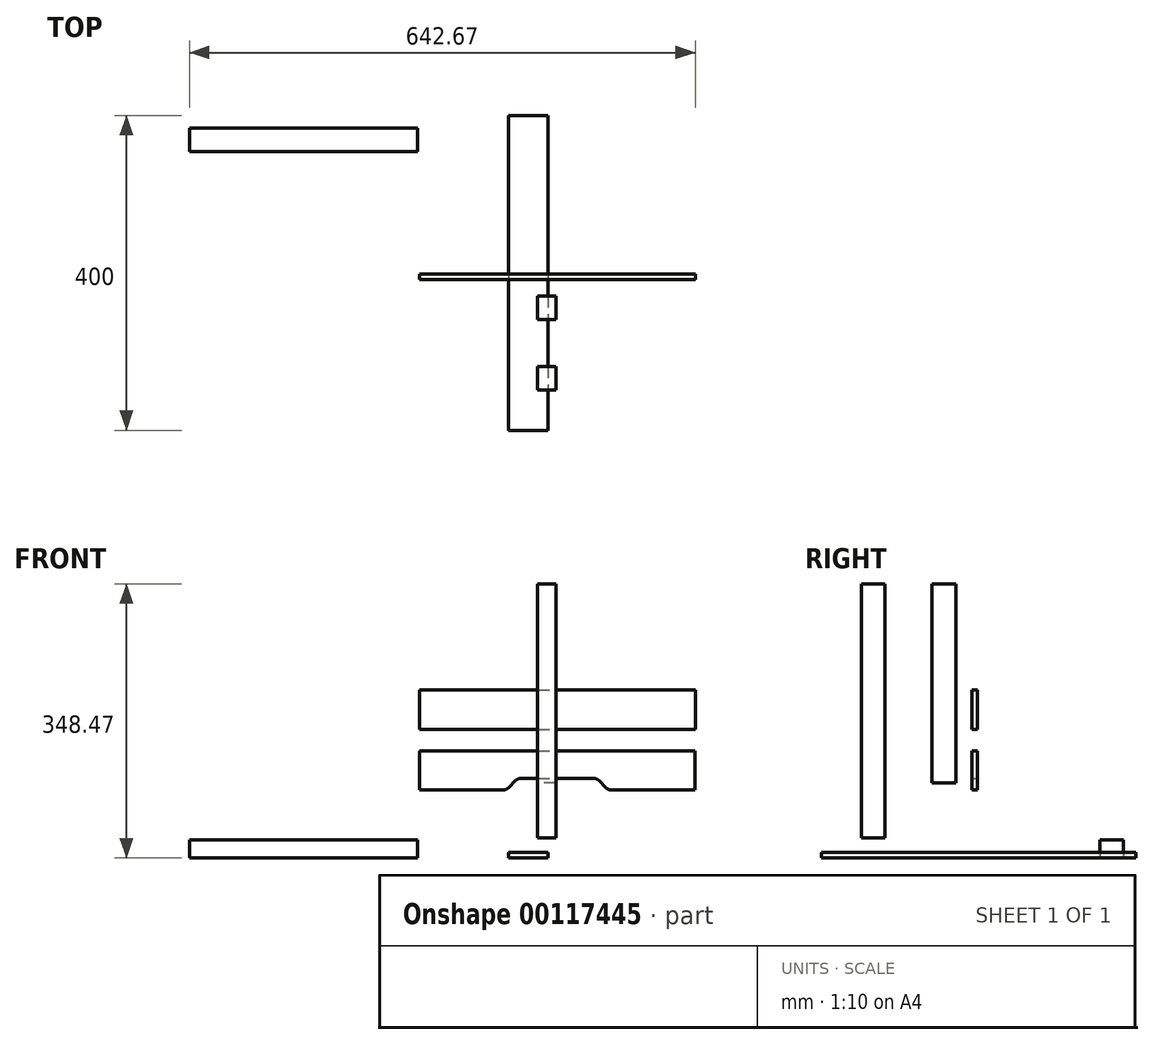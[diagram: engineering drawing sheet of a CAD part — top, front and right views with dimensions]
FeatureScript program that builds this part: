
annotation { "Feature Type Name" : "Feature", "Feature Type Description" : "" }
export const myFeature = defineFeature(function(context is Context, id is Id, definition is map)
    precondition{}
    {
        {
            var Q0;
            Q0=qCreatedBy(makeId("Top.planeOp"),FACE);
            var sketch = newSketch(context, id + "F0", { "sketchPlane" : qUnion([Q0])});
            skLineSegment(sketch, "E0.bottom", {"start": v(-36.82, 201.44) * mm, "end": v(13.18, 201.44) * mm});
            skLineSegment(sketch, "E0.top", {"start": v(-36.82, -198.56) * mm, "end": v(13.18, -198.56) * mm});
            skLineSegment(sketch, "E0.left", {"start": v(-36.82, 201.44) * mm, "end": v(-36.82, -198.56) * mm});
            skLineSegment(sketch, "E0.right", {"start": v(13.18, 201.44) * mm, "end": v(13.18, -198.56) * mm});
            skSolve(sketch);
        }
        {
            var Q0;
            Q0=makeQuery(id+"F2.imprint","IMPRINT",FACE,{"disambiguationData":[TD([[makeQuery(id+"F2.imprint","IMPRINT",EDGE,{"derivedFrom":sQuery(id+"F2.wireOp",EDGE,"E1.bottom")}),-1.0]])]});
            var Q1;
            Q1=makeQuery(id+"F0.imprint","IMPRINT",FACE,{"disambiguationData":[TD([[makeQuery(id+"F0.imprint","IMPRINT",EDGE,{"derivedFrom":sQuery(id+"F0.wireOp",EDGE,"E0.bottom")}),-1.0]])]});
            var Q2;
            Q2=sQuery(id+"F2.wireOp",EDGE,"E1.top");
            extrude(context, id + "F1", {"entities" : qUnion([Q0, Q1]), "surfaceEntities" : qUnion([Q2]), "depth" : 7 * mm});
        }
        {
            var Q0;
            Q0=qCreatedBy(makeId("Front.planeOp"),FACE);
            var sketch = newSketch(context, id + "F2", { "sketchPlane" : qUnion([Q0])});
            skLineSegment(sketch, "E1.bottom", {"start": v(-149.81, 213.54) * mm, "end": v(200.19, 213.54) * mm});
            skLineSegment(sketch, "E1.top", {"start": v(-149.81, 163.54) * mm, "end": v(200.19, 163.54) * mm});
            skLineSegment(sketch, "E1.left", {"start": v(-149.81, 213.54) * mm, "end": v(-149.81, 163.54) * mm});
            skLineSegment(sketch, "E1.right", {"start": v(200.19, 213.54) * mm, "end": v(200.19, 163.54) * mm});
            skLineSegment(sketch, "E2.bottom", {"start": v(-150.22, 136.45) * mm, "end": v(199.78, 136.45) * mm});
            skLineSegment(sketch, "E2.top", {"start": v(-150.22, 86.45) * mm, "end": v(-44.25, 86.45) * mm});
            skLineSegment(sketch, "E2.left", {"start": v(-150.22, 136.45) * mm, "end": v(-150.22, 86.45) * mm});
            skLineSegment(sketch, "E2.right", {"start": v(199.78, 136.45) * mm, "end": v(199.78, 86.38) * mm});
            skLineSegment(sketch, "E3", {"start": v(-37.18, 89.38) * mm, "end": v(-28.04, 98.52) * mm});
            skLineSegment(sketch, "E4", {"start": v(-20.97, 101.45) * mm, "end": v(70.7, 101.45) * mm});
            skLineSegment(sketch, "E5", {"start": v(77.83, 98.46) * mm, "end": v(86.7, 89.44) * mm});
            skLineSegment(sketch, "E6", {"start": v(93.82, 86.45) * mm, "end": v(199.78, 86.38) * mm});
            skPoint(sketch, "E7.visualSharp", {"position": v(-40.11, 86.45) * mm});
            skArc(sketch, "E7.filletArc", {"start": v(-44.25, 86.45) * mm, "mid": v(-40.43, 87.2) * mm, "end": v(-37.18, 89.38) * mm});
            skPoint(sketch, "E8.visualSharp", {"position": v(-25.11, 101.45) * mm});
            skArc(sketch, "E8.filletArc", {"start": v(-20.97, 101.45) * mm, "mid": v(-24.8, 100.69) * mm, "end": v(-28.04, 98.52) * mm});
            skPoint(sketch, "E9.visualSharp", {"position": v(74.89, 101.45) * mm});
            skArc(sketch, "E9.filletArc", {"start": v(77.83, 98.46) * mm, "mid": v(74.56, 100.67) * mm, "end": v(70.7, 101.45) * mm});
            skPoint(sketch, "E10.visualSharp", {"position": v(89.63, 86.45) * mm});
            skArc(sketch, "E10.filletArc", {"start": v(86.7, 89.44) * mm, "mid": v(89.96, 87.22) * mm, "end": v(93.82, 86.45) * mm});
            skSolve(sketch);
        }
        {
            var Q0;
            Q0 = qSketchRegion(id + "F2", true);
            var Q1;
            Q1=sQuery(id+"F2.wireOp",EDGE,"E2.left");
            var Q2;
            Q2=sQuery(id+"F2.wireOp",EDGE,"E2.bottom");
            var Q3;
            Q3=sQuery(id+"F2.wireOp",EDGE,"E2.top");
            var Q4;
            Q4=sQuery(id+"F2.wireOp",EDGE,"E7.filletArc");
            var Q5;
            Q5=sQuery(id+"F2.wireOp",EDGE,"E3");
            var Q6;
            Q6=sQuery(id+"F2.wireOp",EDGE,"E8.filletArc");
            var Q7;
            Q7=sQuery(id+"F2.wireOp",EDGE,"E4");
            var Q8;
            Q8=sQuery(id+"F2.wireOp",EDGE,"E9.filletArc");
            var Q9;
            Q9=sQuery(id+"F2.wireOp",EDGE,"E5");
            var Q10;
            Q10=sQuery(id+"F2.wireOp",EDGE,"E10.filletArc");
            var Q11;
            Q11=sQuery(id+"F2.wireOp",EDGE,"E6");
            var Q12;
            Q12=sQuery(id+"F2.wireOp",EDGE,"E2.right");
            extrude(context, id + "F3", {"entities" : qUnion([Q0]), "surfaceEntities" : qUnion([Q1, Q2, Q3, Q4, Q5, Q6, Q7, Q8, Q9, Q10, Q11, Q12]), "depth" : 7 * mm});
        }
        {
            var Q0;
            Q0=qCreatedBy(makeId("Top.planeOp"),FACE);
            var sketch = newSketch(context, id + "F4", { "sketchPlane" : qUnion([Q0])});
            skLineSegment(sketch, "E11.bottom", {"start": v(-442.48, 185.5) * mm, "end": v(-152.48, 185.5) * mm});
            skLineSegment(sketch, "E11.top", {"start": v(-442.48, 155.5) * mm, "end": v(-152.48, 155.5) * mm});
            skLineSegment(sketch, "E11.left", {"start": v(-442.48, 185.5) * mm, "end": v(-442.48, 155.5) * mm});
            skLineSegment(sketch, "E11.right", {"start": v(-152.48, 185.5) * mm, "end": v(-152.48, 155.5) * mm});
            skSolve(sketch);
        }
        {
            var Q0;
            Q0=makeQuery(id+"F4.imprint","IMPRINT",FACE,{"disambiguationData":[TD([[makeQuery(id+"F4.imprint","IMPRINT",EDGE,{"derivedFrom":sQuery(id+"F4.wireOp",EDGE,"E11.bottom")}),-1.0]])]});
            extrude(context, id + "F5", {"entities" : qUnion([Q0]), "depth" : 23 * mm});
        }
        {
            var Q0;
            Q0=qCreatedBy(makeId("Right.planeOp"),FACE);
            var sketch = newSketch(context, id + "F6", { "sketchPlane" : qUnion([Q0])});
            skLineSegment(sketch, "E12.bottom", {"start": v(-57.74, 348.47) * mm, "end": v(-27.74, 348.47) * mm});
            skLineSegment(sketch, "E12.top", {"start": v(-57.74, 95.47) * mm, "end": v(-27.74, 95.47) * mm});
            skLineSegment(sketch, "E12.left", {"start": v(-57.74, 348.47) * mm, "end": v(-57.74, 95.47) * mm});
            skLineSegment(sketch, "E12.right", {"start": v(-27.74, 348.47) * mm, "end": v(-27.74, 95.47) * mm});
            skLineSegment(sketch, "E13.bottom", {"start": v(-117.32, 348.47) * mm, "end": v(-147.32, 348.47) * mm});
            skLineSegment(sketch, "E13.top", {"start": v(-117.32, 25.47) * mm, "end": v(-147.32, 25.47) * mm});
            skLineSegment(sketch, "E13.left", {"start": v(-117.32, 348.47) * mm, "end": v(-117.32, 25.47) * mm});
            skLineSegment(sketch, "E13.right", {"start": v(-147.32, 348.47) * mm, "end": v(-147.32, 25.47) * mm});
            skSolve(sketch);
        }
        {
            var Q0;
            Q0 = qSketchRegion(id + "F6", true);
            var Q1;
            Q1=makeQuery(id+"F6.imprint","IMPRINT",FACE,{"disambiguationData":[TD([[makeQuery(id+"F6.imprint","IMPRINT",EDGE,{"derivedFrom":sQuery(id+"F6.wireOp",EDGE,"E12.bottom")}),-1.0]])]});
            extrude(context, id + "F7", {"entities" : qUnion([Q0, Q1]), "depth" : 23 * mm});
        }
    });
